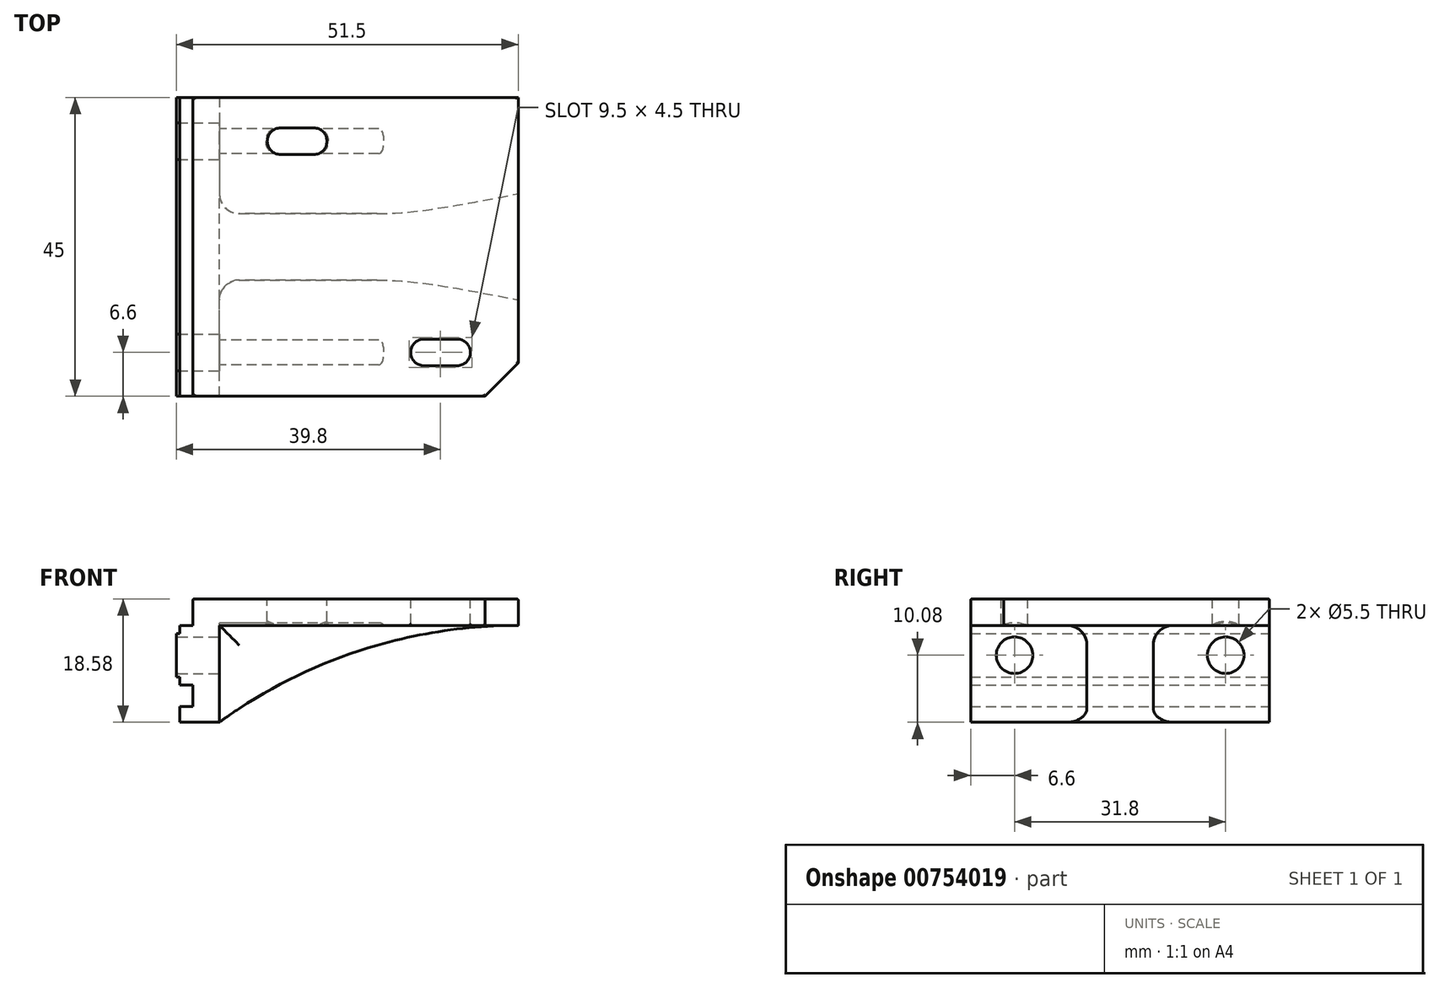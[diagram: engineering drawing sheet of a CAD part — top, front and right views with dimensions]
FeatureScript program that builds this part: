
annotation { "Feature Type Name" : "Feature", "Feature Type Description" : "" }
export const myFeature = defineFeature(function(context is Context, id is Id, definition is map)
    precondition{}
    {
        {
            var Q0;
            Q0=qCreatedBy(makeId("Front.planeOp"),FACE);
            var sketch = newSketch(context, id + "F0", { "sketchPlane" : qUnion([Q0])});
            skLineSegment(sketch, "E0", {"start": v(-0.5, 0) * mm, "end": v(-0.5, 3.25) * mm});
            skLineSegment(sketch, "E1", {"start": v(-0.5, 3.25) * mm, "end": v(0, 3.25) * mm});
            skLineSegment(sketch, "E2", {"start": v(0, 4.5) * mm, "end": v(2, 4.5) * mm});
            skLineSegment(sketch, "E3", {"start": v(2, 4.5) * mm, "end": v(2, 8.5) * mm});
            skLineSegment(sketch, "E4", {"start": v(2, 8.5) * mm, "end": v(6, 8.5) * mm});
            skLineSegment(sketch, "E5", {"start": v(6, 8.5) * mm, "end": v(6, 0) * mm});
            skLineSegment(sketch, "E6", {"start": v(-9.5, 0) * mm, "end": v(-9.5, 3.38) * mm, "construction": true});
            skLineSegment(sketch, "E7", {"start": v(-9.5, 3.38) * mm, "end": v(0, 3.38) * mm, "construction": true});
            skLineSegment(sketch, "E8", {"start": v(0, 3.38) * mm, "end": v(0, 4.87) * mm, "construction": true});
            skLineSegment(sketch, "E9", {"start": v(0, 4.87) * mm, "end": v(1.75, 4.87) * mm, "construction": true});
            skLineSegment(sketch, "E10", {"start": v(1.75, 4.87) * mm, "end": v(1.75, 8.47) * mm, "construction": true});
            skLineSegment(sketch, "E11", {"start": v(1.75, 8.47) * mm, "end": v(-22.36, 8.47) * mm, "construction": true});
            skLineSegment(sketch, "E12", {"start": v(0, 4.5) * mm, "end": v(0, 3.25) * mm});
            skLineSegment(sketch, "E13", {"start": v(-9.5, 0) * mm, "end": v(29.9, 0) * mm, "construction": true});
            skLineSegment(sketch, "E14.MirrorCS", {"start": v(-9.5, 0) * mm, "end": v(-9.5, -3.38) * mm, "construction": true});
            skLineSegment(sketch, "E15.MirrorCS", {"start": v(-9.5, -3.38) * mm, "end": v(0, -3.38) * mm, "construction": true});
            skLineSegment(sketch, "E16", {"start": v(0, -3.38) * mm, "end": v(0, -4.87) * mm, "construction": true});
            skLineSegment(sketch, "E17.MirrorCS", {"start": v(-0.5, 0) * mm, "end": v(-0.5, -3.25) * mm});
            skLineSegment(sketch, "E18.MirrorCS", {"start": v(-0.5, -3.25) * mm, "end": v(0, -3.25) * mm});
            skLineSegment(sketch, "E19", {"start": v(1.75, -4.87) * mm, "end": v(1.75, -7.47) * mm, "construction": true});
            skLineSegment(sketch, "E20", {"start": v(1.75, -7.47) * mm, "end": v(0, -7.47) * mm, "construction": true});
            skLineSegment(sketch, "E21", {"start": v(0, -7.47) * mm, "end": v(0, -10.07) * mm, "construction": true});
            skLineSegment(sketch, "E22", {"start": v(0, -10.07) * mm, "end": v(-21.5, -10.08) * mm, "construction": true});
            skLineSegment(sketch, "E23.MirrorCS", {"start": v(0, -4.5) * mm, "end": v(0, -3.25) * mm});
            skLineSegment(sketch, "E24.MirrorCS", {"start": v(0, -4.5) * mm, "end": v(2, -4.5) * mm});
            skLineSegment(sketch, "E25", {"start": v(2, -4.5) * mm, "end": v(2, -7.75) * mm});
            skLineSegment(sketch, "E26", {"start": v(2, -7.75) * mm, "end": v(0, -7.75) * mm});
            skLineSegment(sketch, "E27", {"start": v(0, -7.75) * mm, "end": v(0, -10.07) * mm});
            skLineSegment(sketch, "E28", {"start": v(0, -10.07) * mm, "end": v(6, -10.07) * mm});
            skLineSegment(sketch, "E29", {"start": v(6, -10.08) * mm, "end": v(6, 0) * mm});
            skLineSegment(sketch, "E30.MirrorCS", {"start": v(0, -4.87) * mm, "end": v(1.75, -4.87) * mm, "construction": true});
            skSolve(sketch);
        }
        {
            var Q0;
            Q0 = qSketchRegion(id + "F0", true);
            extrude(context, id + "F1", {"entities" : qUnion([Q0]), "depth" : 22.5 * mm, "offsetDistance" : 25 * mm, "hasSecondDirection" : true, "secondDirectionOppositeDirection" : true, "secondDirectionDepth" : 22.5 * mm});
        }
        {
            var Q0;
            Q0=makeQuery(id+"F1.opExtrude","SWEPT_FACE",FACE,{"disambiguationData":[OSD([sQuery(id+"F0.wireOp",EDGE,"E5"),sQuery(id+"F0.wireOp",EDGE,"E29")])]});
            cPlane(context, id + "F2", {"entities" : qUnion([Q0]), "cplaneType" : CPlaneType.OFFSET, "offset" : 0 * mm, "width" : 150 * mm, "height" : 150 * mm});
        }
        {
            var Q0;
            Q0=qCreatedBy(makeId("Front.planeOp"),FACE);
            var sketch = newSketch(context, id + "F3", { "sketchPlane" : qUnion([Q0])});
            skLineSegment(sketch, "E31.0", {"start": v(6, 8.5) * mm, "end": v(6, -10.07) * mm});
            skLineSegment(sketch, "E32", {"start": v(6, 8.5) * mm, "end": v(51, 8.5) * mm});
            skLineSegment(sketch, "E33", {"start": v(51, 8.5) * mm, "end": v(51, 4.5) * mm});
            skArc(sketch, "E34", {"start": v(51, 4.5) * mm, "mid": v(27.35, 0.77) * mm, "end": v(6, -10.07) * mm});
            skLineSegment(sketch, "E35", {"start": v(51, 4.5) * mm, "end": v(6, 4.5) * mm, "construction": true});
            skSolve(sketch);
        }
        {
            var Q0;
            Q0 = qSketchRegion(id + "F3", true);
            var Q1;
            Q1=makeQuery(id+"F1.opExtrude","CAP_FACE",FACE,{"disambiguationData":[OSD([sQuery(id+"F0.wireOp",EDGE,"E0"),sQuery(id+"F0.wireOp",EDGE,"E1"),sQuery(id+"F0.wireOp",EDGE,"E2"),sQuery(id+"F0.wireOp",EDGE,"E3"),sQuery(id+"F0.wireOp",EDGE,"E4"),sQuery(id+"F0.wireOp",EDGE,"E5"),sQuery(id+"F0.wireOp",EDGE,"E12"),sQuery(id+"F0.wireOp",EDGE,"E17.MirrorCS"),sQuery(id+"F0.wireOp",EDGE,"E18.MirrorCS"),sQuery(id+"F0.wireOp",EDGE,"E23.MirrorCS"),sQuery(id+"F0.wireOp",EDGE,"E24.MirrorCS"),sQuery(id+"F0.wireOp",EDGE,"E25"),sQuery(id+"F0.wireOp",EDGE,"E26"),sQuery(id+"F0.wireOp",EDGE,"E27"),sQuery(id+"F0.wireOp",EDGE,"E28"),sQuery(id+"F0.wireOp",EDGE,"E29")])],"isStart":false});
            var Q2;
            Q2=makeQuery(id+"F1.opExtrude","CAP_FACE",FACE,{"disambiguationData":[OSD([sQuery(id+"F0.wireOp",EDGE,"E0"),sQuery(id+"F0.wireOp",EDGE,"E1"),sQuery(id+"F0.wireOp",EDGE,"E2"),sQuery(id+"F0.wireOp",EDGE,"E3"),sQuery(id+"F0.wireOp",EDGE,"E4"),sQuery(id+"F0.wireOp",EDGE,"E5"),sQuery(id+"F0.wireOp",EDGE,"E12"),sQuery(id+"F0.wireOp",EDGE,"E17.MirrorCS"),sQuery(id+"F0.wireOp",EDGE,"E18.MirrorCS"),sQuery(id+"F0.wireOp",EDGE,"E23.MirrorCS"),sQuery(id+"F0.wireOp",EDGE,"E24.MirrorCS"),sQuery(id+"F0.wireOp",EDGE,"E25"),sQuery(id+"F0.wireOp",EDGE,"E26"),sQuery(id+"F0.wireOp",EDGE,"E27"),sQuery(id+"F0.wireOp",EDGE,"E28"),sQuery(id+"F0.wireOp",EDGE,"E29")])],"isStart":true});
            extrude(context, id + "F4", {"entities" : qUnion([Q0]), "operationType" : NewBodyOperationType.ADD, "endBound" : BoundingType.UP_TO_SURFACE, "depth" : 25 * mm, "endBoundEntityFace" : qUnion([Q1]), "offsetDistance" : 25 * mm, "hasSecondDirection" : true, "secondDirectionBound" : SecondDirectionBoundingType.UP_TO_SURFACE, "secondDirectionOppositeDirection" : true, "secondDirectionDepth" : 25 * mm, "secondDirectionBoundEntityFace" : qUnion([Q2])});
        }
        {
            var Q0;
            Q0=qCreatedBy(id+"F2.planeOp",FACE);
            var sketch = newSketch(context, id + "F5", { "sketchPlane" : qUnion([Q0])});
            skLineSegment(sketch, "E36.0.0", {"start": v(22.5, 4.5) * mm, "end": v(-22.5, 4.5) * mm, "construction": true});
            skLineSegment(sketch, "E36.0.1", {"start": v(-22.5, 4.5) * mm, "end": v(-22.5, -10.08) * mm, "construction": true});
            skLineSegment(sketch, "E36.0.2", {"start": v(-22.5, -10.08) * mm, "end": v(22.5, -10.08) * mm, "construction": true});
            skLineSegment(sketch, "E36.0.3", {"start": v(22.5, -10.08) * mm, "end": v(22.5, 4.5) * mm, "construction": true});
            skLineSegment(sketch, "E37.bottom", {"start": v(-22.5, 4.5) * mm, "end": v(-5, 4.5) * mm});
            skLineSegment(sketch, "E37.top", {"start": v(-22.5, -10.08) * mm, "end": v(-5, -10.08) * mm});
            skLineSegment(sketch, "E37.left", {"start": v(-22.5, 4.5) * mm, "end": v(-22.5, -10.08) * mm});
            skLineSegment(sketch, "E37.right", {"start": v(-5, 4.5) * mm, "end": v(-5, -10.08) * mm});
            skLineSegment(sketch, "E38.MirrorCS", {"start": v(22.5, 4.5) * mm, "end": v(22.5, -10.08) * mm});
            skLineSegment(sketch, "E39.MirrorCS", {"start": v(5, 4.5) * mm, "end": v(5, -10.08) * mm});
            skLineSegment(sketch, "E40.MirrorCS", {"start": v(22.5, 4.5) * mm, "end": v(5, 4.5) * mm});
            skLineSegment(sketch, "E41.MirrorCS", {"start": v(22.5, -10.08) * mm, "end": v(5, -10.08) * mm});
            skSolve(sketch);
        }
        {
            var Q0;
            Q0 = qSketchRegion(id + "F5", true);
            extrude(context, id + "F6", {"entities" : qUnion([Q0]), "operationType" : NewBodyOperationType.REMOVE, "endBound" : BoundingType.THROUGH_ALL, "depth" : 25 * mm, "offsetDistance" : 25 * mm});
        }
        {
            var Q0;
            Q0=qCreatedBy(id+"F2.planeOp",FACE);
            var sketch = newSketch(context, id + "F7", { "sketchPlane" : qUnion([Q0])});
            skCircle(sketch, "E42", {"center": v(-15.9, 0) * mm, "radius": 2.75 * mm});
            skCircle(sketch, "E43.MirrorC", {"center": v(15.9, 0) * mm, "radius": 2.75 * mm});
            skSolve(sketch);
        }
        {
            var Q0;
            Q0 = qSketchRegion(id + "F7", true);
            extrude(context, id + "F8", {"entities" : qUnion([Q0]), "operationType" : NewBodyOperationType.REMOVE, "endBound" : BoundingType.THROUGH_ALL, "oppositeDirection" : true, "depth" : 25 * mm, "offsetDistance" : 25 * mm});
        }
        {
            var Q0;
            Q0=qCreatedBy(id+"F2.planeOp",FACE);
            var sketch = newSketch(context, id + "F9", { "sketchPlane" : qUnion([Q0])});
            skCircle(sketch, "E44", {"center": v(-15.9, 0) * mm, "radius": 4.88 * mm});
            skCircle(sketch, "E45.0", {"center": v(-15.9, 0) * mm, "radius": 2.75 * mm, "construction": true});
            skCircle(sketch, "E46.MirrorC", {"center": v(15.9, 0) * mm, "radius": 4.88 * mm});
            skSolve(sketch);
        }
        {
            var Q0;
            Q0 = qSketchRegion(id + "F9", true);
            extrude(context, id + "F10", {"entities" : qUnion([Q0]), "operationType" : NewBodyOperationType.REMOVE, "depth" : 25 * mm, "offsetDistance" : 25 * mm});
        }
        {
            var Q0;
            Q0=makeQuery(id+"F4.boolean.opBoolean","MERGE",FACE,{"derivedFrom":[makeQuery(id+"F1.opExtrude","SWEPT_FACE",FACE,{"disambiguationData":[OSD([sQuery(id+"F0.wireOp",EDGE,"E4")])]}),makeQuery(id+"F4.opExtrude","SWEPT_FACE",FACE,{"disambiguationData":[OSD([sQuery(id+"F3.wireOp",EDGE,"E32")])]})]});
            var sketch = newSketch(context, id + "F11", { "sketchPlane" : qUnion([Q0])});
            skLineSegment(sketch, "E47.bottom", {"start": v(17.7, 15.9) * mm, "end": v(39.3, 15.9) * mm, "construction": true});
            skLineSegment(sketch, "E47.top", {"start": v(17.7, -15.9) * mm, "end": v(39.3, -15.9) * mm, "construction": true});
            skLineSegment(sketch, "E47.left", {"start": v(17.7, 15.9) * mm, "end": v(17.7, -15.9) * mm, "construction": true});
            skLineSegment(sketch, "E47.right", {"start": v(39.3, 15.9) * mm, "end": v(39.3, -15.9) * mm, "construction": true});
            skLineSegment(sketch, "E48", {"start": v(17.7, 0) * mm, "end": v(39.3, 0) * mm, "construction": true});
            skLineSegment(sketch, "E49.bottom", {"start": v(6, 22.5) * mm, "end": v(51, 22.5) * mm, "construction": true});
            skLineSegment(sketch, "E49.top", {"start": v(6, -22.5) * mm, "end": v(51, -22.5) * mm, "construction": true});
            skLineSegment(sketch, "E49.left", {"start": v(6, 22.5) * mm, "end": v(6, -22.5) * mm, "construction": true});
            skLineSegment(sketch, "E49.right", {"start": v(51, 22.5) * mm, "end": v(51, -22.5) * mm, "construction": true});
            skLineSegment(sketch, "E50", {"start": v(6, 0) * mm, "end": v(51, 0) * mm, "construction": true});
            skLineSegment(sketch, "E51", {"start": v(28.5, 22.5) * mm, "end": v(28.5, -22.5) * mm, "construction": true});
            skLineSegment(sketch, "E52", {"start": v(28.5, 15.9) * mm, "end": v(28.5, -15.9) * mm, "construction": true});
            skLineSegment(sketch, "E53", {"start": v(15.2, 15.9) * mm, "end": v(20.2, 15.9) * mm, "construction": true});
            skArc(sketch, "E54.0.startCap", {"start": v(15.2, 13.9) * mm, "mid": v(13.2, 15.9) * mm, "end": v(15.2, 17.9) * mm});
            skArc(sketch, "E54.0.endCap", {"start": v(20.2, 17.9) * mm, "mid": v(22.2, 15.9) * mm, "end": v(20.2, 13.9) * mm});
            skLineSegment(sketch, "E54.0.left", {"start": v(15.2, 17.9) * mm, "end": v(20.2, 17.9) * mm});
            skLineSegment(sketch, "E54.0.right", {"start": v(15.2, 13.9) * mm, "end": v(20.2, 13.9) * mm});
            skLineSegment(sketch, "E55", {"start": v(36.8, -15.9) * mm, "end": v(41.8, -15.9) * mm, "construction": true});
            skArc(sketch, "E56.0.startCap", {"start": v(36.8, -17.9) * mm, "mid": v(34.8, -15.9) * mm, "end": v(36.8, -13.9) * mm});
            skArc(sketch, "E56.0.endCap", {"start": v(41.8, -13.9) * mm, "mid": v(43.8, -15.9) * mm, "end": v(41.8, -17.9) * mm});
            skLineSegment(sketch, "E56.0.left", {"start": v(36.8, -13.9) * mm, "end": v(41.8, -13.9) * mm});
            skLineSegment(sketch, "E56.0.right", {"start": v(36.8, -17.9) * mm, "end": v(41.8, -17.9) * mm});
            skSolve(sketch);
        }
        {
            var Q0;
            Q0 = qSketchRegion(id + "F11", true);
            extrude(context, id + "F12", {"entities" : qUnion([Q0]), "operationType" : NewBodyOperationType.REMOVE, "endBound" : BoundingType.THROUGH_ALL, "oppositeDirection" : true, "depth" : 25 * mm, "offsetDistance" : 25 * mm});
        }
        {
            var Q0;
            Q0=makeQuery(id+"F4.boolean.opBoolean","MERGE",FACE,{"derivedFrom":[makeQuery(id+"F1.opExtrude","SWEPT_FACE",FACE,{"disambiguationData":[OSD([sQuery(id+"F0.wireOp",EDGE,"E4")])]}),makeQuery(id+"F4.opExtrude","SWEPT_FACE",FACE,{"disambiguationData":[OSD([sQuery(id+"F3.wireOp",EDGE,"E32")])]})]});
            var sketch = newSketch(context, id + "F13", { "sketchPlane" : qUnion([Q0])});
            skLineSegment(sketch, "E57", {"start": v(51, -17.5) * mm, "end": v(51, -22.5) * mm});
            skLineSegment(sketch, "E58", {"start": v(51, -22.5) * mm, "end": v(46, -22.5) * mm});
            skLineSegment(sketch, "E59", {"start": v(46, -22.5) * mm, "end": v(51, -17.5) * mm});
            skSolve(sketch);
        }
        {
            var Q0;
            Q0 = qSketchRegion(id + "F13", true);
            extrude(context, id + "F14", {"entities" : qUnion([Q0]), "operationType" : NewBodyOperationType.REMOVE, "endBound" : BoundingType.THROUGH_ALL, "oppositeDirection" : true, "depth" : 25 * mm, "offsetDistance" : 25 * mm});
        }
        {
            var Q0;
            Q0=makeQuery(id+"F4.boolean.opBoolean","MERGE",FACE,{"derivedFrom":[makeQuery(id+"F1.opExtrude","SWEPT_FACE",FACE,{"disambiguationData":[OSD([sQuery(id+"F0.wireOp",EDGE,"E4")])]}),makeQuery(id+"F4.opExtrude","SWEPT_FACE",FACE,{"disambiguationData":[OSD([sQuery(id+"F3.wireOp",EDGE,"E32")])]})]});
            var Q1;
            Q1=makeQuery(id+"F12.boolean.opBoolean","INTERSECT",EDGE,{"derivedFrom":[makeQuery(id+"F6.boolean.opBoolean","COPY",FACE,{"derivedFrom":makeQuery(id+"F6.opExtrude","SWEPT_FACE",FACE,{"disambiguationData":[OSD([sQuery(id+"F5.wireOp",EDGE,"E40.MirrorCS")])]})}),makeQuery(id+"F12.opExtrude","SWEPT_FACE",FACE,{"disambiguationData":[OSD([sQuery(id+"F11.wireOp",EDGE,"E54.0.endCap")])]})]});
            var Q2;
            Q2=makeQuery(id+"F12.boolean.opBoolean","INTERSECT",EDGE,{"derivedFrom":[makeQuery(id+"F6.boolean.opBoolean","COPY",FACE,{"derivedFrom":makeQuery(id+"F6.opExtrude","SWEPT_FACE",FACE,{"disambiguationData":[OSD([sQuery(id+"F5.wireOp",EDGE,"E37.bottom")])]})}),makeQuery(id+"F12.opExtrude","SWEPT_FACE",FACE,{"disambiguationData":[OSD([sQuery(id+"F11.wireOp",EDGE,"E56.0.endCap")])]})]});
            var Q3;
            {var subQ0=sQuery(id+"F3.wireOp",EDGE,"E33");var subQ1=sQuery(id+"F3.wireOp",EDGE,"E34");Q3=makeQuery(id+"F6.boolean.opBoolean","SPLIT",EDGE,{"disambiguationData":[topologyDisambiguationEdgeConnected([makeQuery(id+"F4.opExtrude","SWEPT_FACE",FACE,{"disambiguationData":[OSD([subQ1])]})])],"derivedFrom":makeQuery(id+"F4.opExtrude","TWEAK_EDGE",EDGE,{"derivedFrom":[makeQuery(id+"F3.imprint","IMPRINT",EDGE,{"derivedFrom":subQ0}),makeQuery(id+"F3.imprint","IMPRINT",EDGE,{"derivedFrom":subQ1})]})});}
            var Q4;
            {var subQ0=sQuery(id+"F3.wireOp",EDGE,"E33");Q4=makeQuery(id+"F6.boolean.opBoolean","SPLIT",EDGE,{"disambiguationData":[topologyDisambiguationEdgeConnected([makeQuery(id+"F6.opExtrude","SWEPT_FACE",FACE,{"disambiguationData":[OSD([sQuery(id+"F5.wireOp",EDGE,"E40.MirrorCS")])]})])],"derivedFrom":makeQuery(id+"F4.opExtrude","TWEAK_EDGE",EDGE,{"derivedFrom":[makeQuery(id+"F3.imprint","IMPRINT",EDGE,{"derivedFrom":subQ0}),makeQuery(id+"F3.imprint","IMPRINT",EDGE,{"derivedFrom":sQuery(id+"F3.wireOp",EDGE,"E34")})]})});}
            var Q5;
            {var subQ0=sQuery(id+"F3.wireOp",EDGE,"E33");Q5=makeQuery(id+"F6.boolean.opBoolean","SPLIT",EDGE,{"disambiguationData":[topologyDisambiguationEdgeConnected([makeQuery(id+"F6.opExtrude","SWEPT_FACE",FACE,{"disambiguationData":[OSD([sQuery(id+"F5.wireOp",EDGE,"E37.bottom")])]})])],"derivedFrom":makeQuery(id+"F4.opExtrude","TWEAK_EDGE",EDGE,{"derivedFrom":[makeQuery(id+"F3.imprint","IMPRINT",EDGE,{"derivedFrom":subQ0}),makeQuery(id+"F3.imprint","IMPRINT",EDGE,{"derivedFrom":sQuery(id+"F3.wireOp",EDGE,"E34")})]})});}
            var Q6;
            Q6=makeQuery(id+"F6.boolean.opBoolean","COPY",EDGE,{"derivedFrom":makeQuery(id+"F6.opExtrude","SWEPT_EDGE",EDGE,{"disambiguationData":[OSD([sQuery(id+"F5.wireOp",EDGE,"E38.MirrorCS"),sQuery(id+"F5.wireOp",EDGE,"E40.MirrorCS")])]})});
            var Q7;
            Q7=makeQuery(id+"F14.boolean.opBoolean","INTERSECT",EDGE,{"derivedFrom":[makeQuery(id+"F6.boolean.opBoolean","COPY",FACE,{"derivedFrom":makeQuery(id+"F6.opExtrude","SWEPT_FACE",FACE,{"disambiguationData":[OSD([sQuery(id+"F5.wireOp",EDGE,"E37.bottom")])]})}),makeQuery(id+"F14.opExtrude","SWEPT_FACE",FACE,{"disambiguationData":[OSD([sQuery(id+"F13.wireOp",EDGE,"E59")])]})]});
            var Q8;
            Q8=makeQuery(id+"F6.boolean.opBoolean","COPY",EDGE,{"derivedFrom":makeQuery(id+"F6.opExtrude","SWEPT_EDGE",EDGE,{"disambiguationData":[OSD([sQuery(id+"F5.wireOp",EDGE,"E37.bottom"),sQuery(id+"F5.wireOp",EDGE,"E37.left")])]})});
            var Q9;
            Q9=makeQuery(id+"F12.boolean.opBoolean","INTERSECT",EDGE,{"derivedFrom":[makeQuery(id+"F10.boolean.opBoolean","COPY",FACE,{"derivedFrom":makeQuery(id+"F10.opExtrude","SWEPT_FACE",FACE,{"disambiguationData":[OSD([sQuery(id+"F9.wireOp",EDGE,"E46.MirrorC")])]})}),makeQuery(id+"F12.opExtrude","SWEPT_FACE",FACE,{"disambiguationData":[OSD([sQuery(id+"F11.wireOp",EDGE,"E54.0.endCap")])]})]});
            var Q10;
            Q10=makeQuery(id+"F12.boolean.opBoolean","INTERSECT",EDGE,{"derivedFrom":[makeQuery(id+"F10.boolean.opBoolean","COPY",FACE,{"derivedFrom":makeQuery(id+"F10.opExtrude","SWEPT_FACE",FACE,{"disambiguationData":[OSD([sQuery(id+"F9.wireOp",EDGE,"E46.MirrorC")])]})}),makeQuery(id+"F12.opExtrude","SWEPT_FACE",FACE,{"disambiguationData":[OSD([sQuery(id+"F11.wireOp",EDGE,"E54.0.startCap")])]})]});
            var Q11;
            Q11=makeQuery(id+"F8.boolean.opBoolean","COPY",EDGE,{"derivedFrom":makeQuery(id+"F8.opExtrude","CAP_EDGE",EDGE,{"disambiguationData":[OSD([sQuery(id+"F7.wireOp",EDGE,"E42")])],"isStart":true})});
            var Q12;
            Q12=makeQuery(id+"F8.boolean.opBoolean","COPY",EDGE,{"derivedFrom":makeQuery(id+"F8.opExtrude","CAP_EDGE",EDGE,{"disambiguationData":[OSD([sQuery(id+"F7.wireOp",EDGE,"E43.MirrorC")])],"isStart":true})});
            var Q13;
            Q13=makeQuery(id+"F8.boolean.opBoolean","INTERSECT",EDGE,{"derivedFrom":[makeQuery(id+"F1.opExtrude","SWEPT_FACE",FACE,{"disambiguationData":[OSD([sQuery(id+"F0.wireOp",EDGE,"E0"),sQuery(id+"F0.wireOp",EDGE,"E17.MirrorCS")])]}),makeQuery(id+"F8.opExtrude","SWEPT_FACE",FACE,{"disambiguationData":[OSD([sQuery(id+"F7.wireOp",EDGE,"E43.MirrorC")])]})]});
            var Q14;
            Q14=makeQuery(id+"F8.boolean.opBoolean","INTERSECT",EDGE,{"derivedFrom":[makeQuery(id+"F1.opExtrude","SWEPT_FACE",FACE,{"disambiguationData":[OSD([sQuery(id+"F0.wireOp",EDGE,"E0"),sQuery(id+"F0.wireOp",EDGE,"E17.MirrorCS")])]}),makeQuery(id+"F8.opExtrude","SWEPT_FACE",FACE,{"disambiguationData":[OSD([sQuery(id+"F7.wireOp",EDGE,"E42")])]})]});
            var Q15;
            Q15=makeQuery(id+"F6.boolean.opBoolean","COPY",EDGE,{"derivedFrom":makeQuery(id+"F6.opExtrude","CAP_EDGE",EDGE,{"disambiguationData":[OSD([sQuery(id+"F5.wireOp",EDGE,"E37.left")])],"isStart":true})});
            var Q16;
            Q16=makeQuery(id+"F6.boolean.opBoolean","COPY",EDGE,{"derivedFrom":makeQuery(id+"F6.opExtrude","CAP_EDGE",EDGE,{"disambiguationData":[OSD([sQuery(id+"F5.wireOp",EDGE,"E38.MirrorCS")])],"isStart":true})});
            fillet(context, id + "F15", {"entities" : qUnion([Q0, Q1, Q2, Q3, Q4, Q5, Q6, Q7, Q8, Q9, Q10, Q11, Q12, Q13, Q14, Q15, Q16]), "radius" : 0.25 * mm, "tangentPropagation" : true, "allowEdgeOverflow" : false});
        }
        {
            var Q0;
            Q0=makeQuery(id+"F6.boolean.opBoolean","COPY",EDGE,{"derivedFrom":makeQuery(id+"F6.opExtrude","SWEPT_EDGE",EDGE,{"disambiguationData":[OSD([sQuery(id+"F5.wireOp",EDGE,"E37.bottom"),sQuery(id+"F5.wireOp",EDGE,"E37.right")])]})});
            var Q1;
            Q1=makeQuery(id+"F6.boolean.opBoolean","COPY",EDGE,{"derivedFrom":makeQuery(id+"F6.opExtrude","CAP_EDGE",EDGE,{"disambiguationData":[OSD([sQuery(id+"F5.wireOp",EDGE,"E37.right")])],"isStart":true})});
            var Q2;
            Q2=makeQuery(id+"F6.boolean.opBoolean","COPY",EDGE,{"derivedFrom":makeQuery(id+"F6.opExtrude","CAP_EDGE",EDGE,{"disambiguationData":[OSD([sQuery(id+"F5.wireOp",EDGE,"E39.MirrorCS")])],"isStart":true})});
            var Q3;
            Q3=makeQuery(id+"F6.boolean.opBoolean","COPY",EDGE,{"derivedFrom":makeQuery(id+"F6.opExtrude","SWEPT_EDGE",EDGE,{"disambiguationData":[OSD([sQuery(id+"F5.wireOp",EDGE,"E39.MirrorCS"),sQuery(id+"F5.wireOp",EDGE,"E40.MirrorCS")])]})});
            fillet(context, id + "F16", {"entities" : qUnion([Q0, Q1, Q2, Q3]), "radius" : 3 * mm, "tangentPropagation" : true, "allowEdgeOverflow" : false});
        }
        {
            var Q0;
            Q0=makeQuery(id+"F10.boolean.opBoolean","COPY",EDGE,{"derivedFrom":makeQuery(id+"F10.opExtrude","CAP_EDGE",EDGE,{"disambiguationData":[OSD([sQuery(id+"F9.wireOp",EDGE,"E44")])],"isStart":false})});
            var Q1;
            Q1=makeQuery(id+"F10.boolean.opBoolean","COPY",EDGE,{"derivedFrom":makeQuery(id+"F10.opExtrude","CAP_EDGE",EDGE,{"disambiguationData":[OSD([sQuery(id+"F9.wireOp",EDGE,"E46.MirrorC")])],"isStart":false})});
            fillet(context, id + "F17", {"entities" : qUnion([Q0, Q1]), "radius" : 1 * mm, "tangentPropagation" : true, "allowEdgeOverflow" : false});
        }
    });
